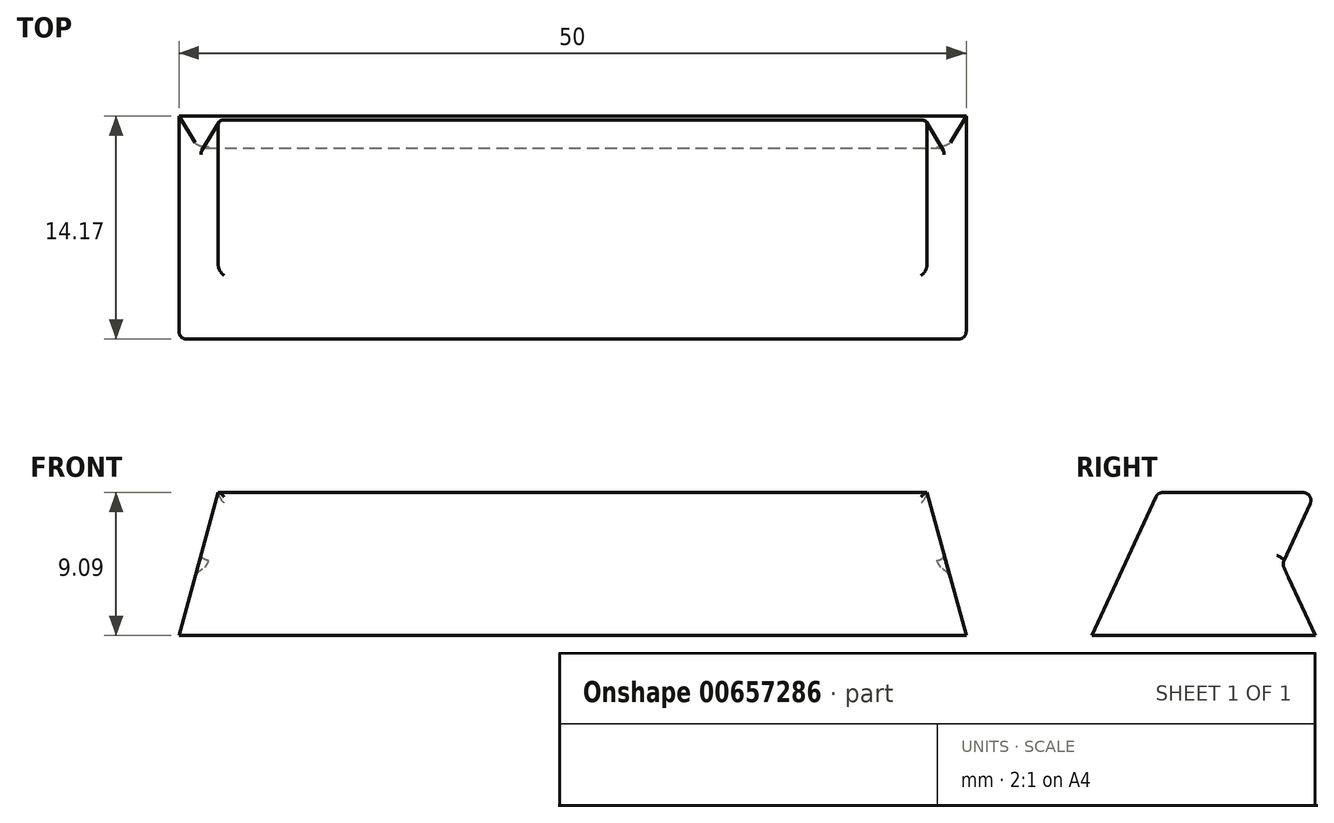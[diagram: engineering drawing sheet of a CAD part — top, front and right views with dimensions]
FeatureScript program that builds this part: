
annotation { "Feature Type Name" : "Feature", "Feature Type Description" : "" }
export const myFeature = defineFeature(function(context is Context, id is Id, definition is map)
    precondition{}
    {
        {
            var Q0;
            Q0=qCreatedBy(makeId("Right.planeOp"),FACE);
            var sketch = newSketch(context, id + "F0", { "sketchPlane" : qUnion([Q0])});
            skLineSegment(sketch, "E0", {"start": v(0, 0) * mm, "end": v(4.17, 9.09) * mm});
            skLineSegment(sketch, "E1", {"start": v(4.17, 9.09) * mm, "end": v(14.17, 9.09) * mm});
            skLineSegment(sketch, "E2", {"start": v(14.17, 9.09) * mm, "end": v(12.09, 4.54) * mm});
            skLineSegment(sketch, "E3", {"start": v(12.09, 4.54) * mm, "end": v(14.17, 0) * mm});
            skLineSegment(sketch, "E4", {"start": v(14.17, 0) * mm, "end": v(0, 0) * mm});
            skSolve(sketch);
        }
        {
            var Q0;
            Q0=makeQuery(id+"F0.imprint","IMPRINT",FACE,{"disambiguationData":[TD([[makeQuery(id+"F0.imprint","IMPRINT",EDGE,{"derivedFrom":sQuery(id+"F0.wireOp",EDGE,"E0")}),-1.0]])]});
            extrude(context, id + "F1", {"entities" : qUnion([Q0]), "depth" : 25 * mm, "offsetDistance" : 25 * mm});
        }
        {
            var Q0;
            Q0=qCreatedBy(makeId("Front.planeOp"),FACE);
            var sketch = newSketch(context, id + "F2", { "sketchPlane" : qUnion([Q0])});
            skLineSegment(sketch, "E5", {"start": v(25, 0) * mm, "end": v(25, 9.09) * mm});
            skLineSegment(sketch, "E6", {"start": v(25, 9.09) * mm, "end": v(22.5, 9.09) * mm});
            skLineSegment(sketch, "E7", {"start": v(22.5, 9.09) * mm, "end": v(25, 0) * mm});
            skSolve(sketch);
        }
        {
            var Q0;
            Q0=makeQuery(id+"F2.imprint","IMPRINT",FACE,{"disambiguationData":[TD([[makeQuery(id+"F2.imprint","IMPRINT",EDGE,{"derivedFrom":sQuery(id+"F2.wireOp",EDGE,"E5")}),1.0]])]});
            extrude(context, id + "F3", {"entities" : qUnion([Q0]), "operationType" : NewBodyOperationType.REMOVE, "endBound" : BoundingType.THROUGH_ALL, "oppositeDirection" : true, "depth" : 25 * mm, "offsetDistance" : 25 * mm});
        }
        {
            var Q0;
            {var subQ0=makeQuery(id+"F1.opExtrude","SWEPT_EDGE",EDGE,{"disambiguationData":[OSD([sQuery(id+"F0.wireOp",EDGE,"E1"),sQuery(id+"F0.wireOp",EDGE,"E2")])]});Q0=makeQuery(id+"F5.boolean.opBoolean","MERGE",EDGE,{"derivedFrom":[subQ0,makeQuery(id+"F5.opPattern","COPY",EDGE,{"derivedFrom":subQ0,"instanceName":"1"})]});}
            var Q1;
            {var subQ0=makeQuery(id+"F1.opExtrude","SWEPT_EDGE",EDGE,{"disambiguationData":[OSD([sQuery(id+"F0.wireOp",EDGE,"E2"),sQuery(id+"F0.wireOp",EDGE,"E3")])]});Q1=makeQuery(id+"F5.boolean.opBoolean","MERGE",EDGE,{"derivedFrom":[subQ0,makeQuery(id+"F5.opPattern","COPY",EDGE,{"derivedFrom":subQ0,"instanceName":"1"})]});}
            var Q2;
            Q2=makeQuery(id+"F3.boolean.opBoolean","COPY",EDGE,{"derivedFrom":makeQuery(id+"F3.opExtrude","SWEPT_EDGE",EDGE,{"disambiguationData":[OSD([sQuery(id+"F2.wireOp",EDGE,"E6"),sQuery(id+"F2.wireOp",EDGE,"E7")])]})});
            var Q3;
            Q3=makeQuery(id+"F3.boolean.opBoolean","INTERSECT",EDGE,{"derivedFrom":[makeQuery(id+"F1.opExtrude","SWEPT_FACE",FACE,{"disambiguationData":[OSD([sQuery(id+"F0.wireOp",EDGE,"E2")])]}),makeQuery(id+"F3.opExtrude","SWEPT_FACE",FACE,{"disambiguationData":[OSD([sQuery(id+"F2.wireOp",EDGE,"E7")])]})]});
            var Q4;
            Q4=makeQuery(id+"F3.boolean.opBoolean","INTERSECT",EDGE,{"derivedFrom":[makeQuery(id+"F1.opExtrude","SWEPT_FACE",FACE,{"disambiguationData":[OSD([sQuery(id+"F0.wireOp",EDGE,"E0")])]}),makeQuery(id+"F3.opExtrude","SWEPT_FACE",FACE,{"disambiguationData":[OSD([sQuery(id+"F2.wireOp",EDGE,"E7")])]})]});
            var Q5;
            Q5=makeQuery(id+"F1.opExtrude","SWEPT_EDGE",EDGE,{"disambiguationData":[OSD([sQuery(id+"F0.wireOp",EDGE,"E0"),sQuery(id+"F0.wireOp",EDGE,"E1")])]});
            fillet(context, id + "F4", {"entities" : qUnion([Q0, Q1, Q2, Q3, Q4, Q5]), "radius" : .5 * mm, "tangentPropagation" : true, "allowEdgeOverflow" : false});
        }
        {
            var Q0;
            Q0=makeQuery(id+"F1.opExtrude","SWEPT_BODY",BODY,{"disambiguationData":[OSD([sQuery(id+"F0.wireOp",EDGE,"E0"),sQuery(id+"F0.wireOp",EDGE,"E1"),sQuery(id+"F0.wireOp",EDGE,"E2"),sQuery(id+"F0.wireOp",EDGE,"E3"),sQuery(id+"F0.wireOp",EDGE,"E4")])]});
            var Q1;
            Q1=makeQuery(id+"F1.opExtrude","CAP_FACE",FACE,{"disambiguationData":[OSD([sQuery(id+"F0.wireOp",EDGE,"E0"),sQuery(id+"F0.wireOp",EDGE,"E1"),sQuery(id+"F0.wireOp",EDGE,"E2"),sQuery(id+"F0.wireOp",EDGE,"E3"),sQuery(id+"F0.wireOp",EDGE,"E4")])],"isStart":true});
            mirror(context, id + "F5", {"operationType" : NewBodyOperationType.ADD, "entities" : qUnion([Q0]), "mirrorPlane" : qUnion([Q1])});
        }
    });
